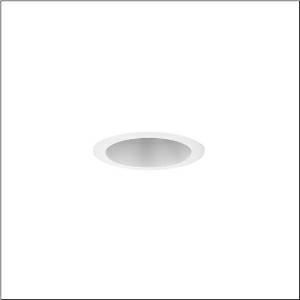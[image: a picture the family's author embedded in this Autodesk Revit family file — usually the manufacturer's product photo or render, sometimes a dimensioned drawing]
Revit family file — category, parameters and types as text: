
# Revit family: lunis_31_mini_51dn167e31
name_source: partatom
category: Lighting Fixtures
units: mm (PartAtom-declared; Revit-internal decimal feet)

## family parameters
Cut with Voids When Loaded = No
Host = Face
Light Source = No
Part Type = Normal
Room Calculation Point = No
Round Connector Dimension = Use Diameter
Shared = No

## types (1)
- Lunis 31 mini (1 x LED, 1000 lm, 8.3 W, 3000K)
    Apparent Load = 8 VA
    CIE Flux Codes = 69 93 99 100 100
    Color Rendering = 80
    Color Temperature = 3000K
    Default Elevation = 1800 mm
    Description = Lunis 31,  mini, downlight, light control with reflector, light emission: direct distribution, LED rated luminous flux: 1.000lm, light colour: 830, mains connection: 220..240V, AC, 50/60Hz, housing, white, protection rating (complete): IP20, protection rating (on room side): IP54, insulation class (complete): insulation class II (safety insulation), certification: CE, packaging unit: 1 piece
    Height = 0 mm  [stored 0 ft]
    Lamp = 1 x LED
    Lamp Light Flux = 1000 lm
    Lamp Power = 8.3 W
    Lamp count = 1
    Length = 188 mm  [stored 0.616798 ft]
    Luminous efficacy = 120 lm/W
    Manufacturer = Siteco
    ModVariant = No
    Model = 51DN167E31
    Mounting Place = Ceiling
    Mounting Type = Recessed
    Number of Poles = 1
    OnlyDefault = Yes
    Power Factor = 1
    Product Name = Lunis 31 mini
    Product group = downlight
    ProductGroupID = 400
    Protection Class = Protection class II
    Protection Degree = IP 20
    RLX_Detail_Level = 1
    RLX_Emergency_Light_Flux = 0 lm
    RLX_Emergency_Type = 0
    RLX_Emergency_Type_DB = No
    RlxData = <blob elided: 21761 chars, md5=46011115>
    Socket = socket
    Standby Power = 0 W
    System Light Flux = 1000 lm
    System Power = 8 W
    Type Comments = Product without accessories
    Type Image = l_1345911.jpg
    URL = http://relux.com
    VarID = ---
    Voltage = 0 V
    Weight = 0.00 kg
    Width = 0 mm  [stored 0 ft]

note: [stored X ft] marks values corroborated as IEEE doubles in the binary element streams (Revit-internal decimal feet)

## geometry (parser evidence)
native form markers: Blend x4, Sweep x9
no freeform markers — native parametric forms only
